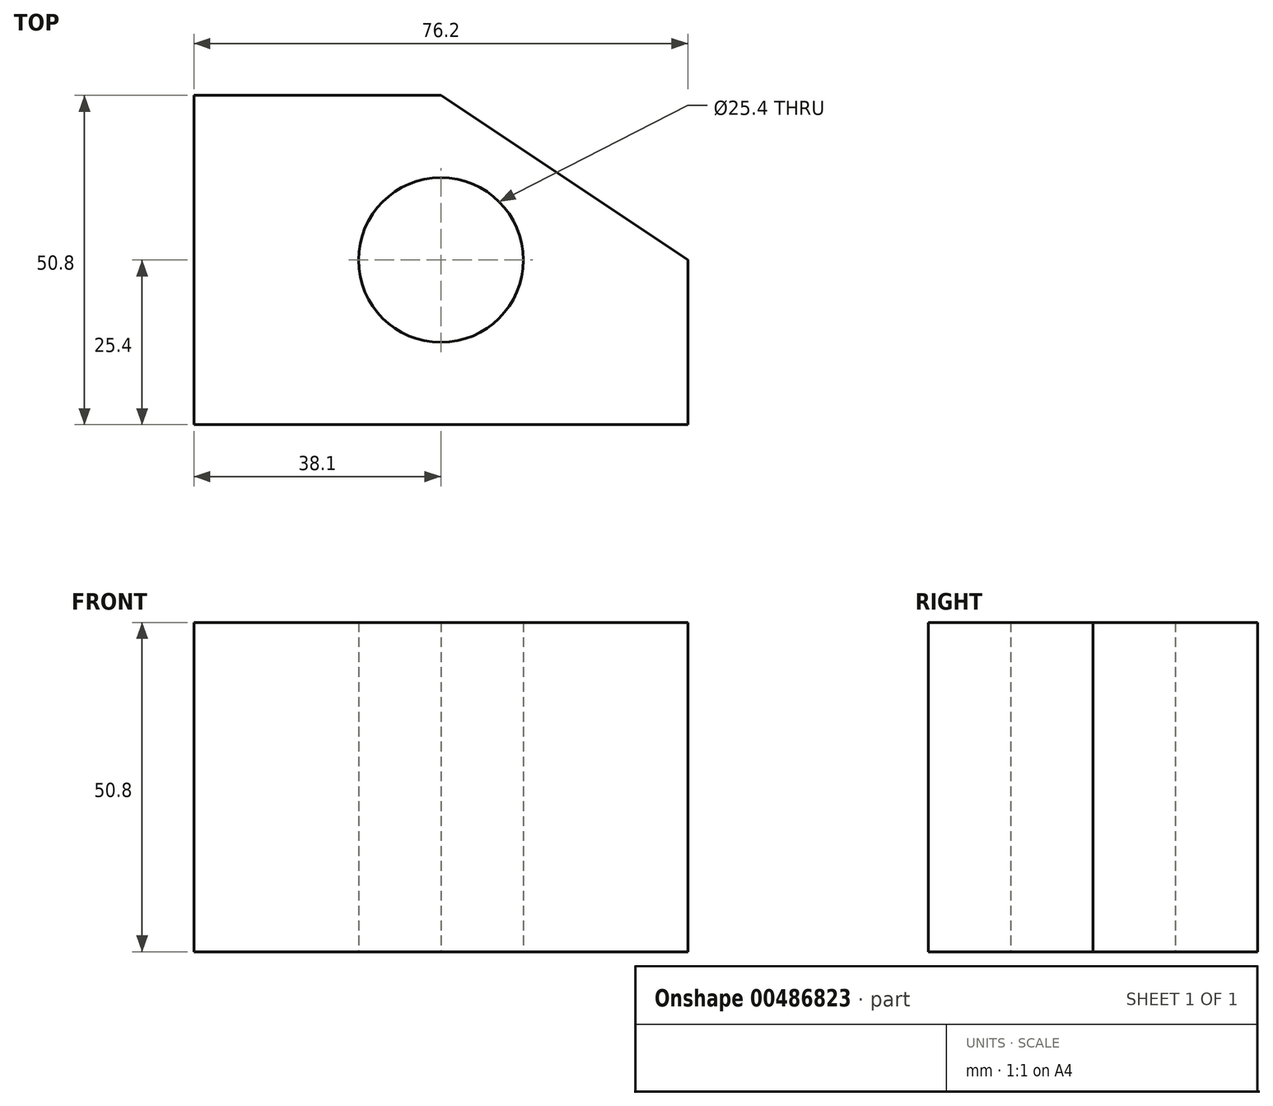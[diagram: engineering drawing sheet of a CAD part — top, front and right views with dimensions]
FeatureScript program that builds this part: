
annotation { "Feature Type Name" : "Feature", "Feature Type Description" : "" }
export const myFeature = defineFeature(function(context is Context, id is Id, definition is map)
    precondition{}
    {
        {
            var Q0;
            Q0=qCreatedBy(makeId("Top.planeOp"),FACE);
            var sketch = newSketch(context, id + "F0", { "sketchPlane" : qUnion([Q0])});
            skLineSegment(sketch, "E0.bottom", {"start": v(0, 0) * mm, "end": v(76.2, 0) * mm});
            skLineSegment(sketch, "E0.left", {"start": v(0, 0) * mm, "end": v(0, 25.4) * mm});
            skLineSegment(sketch, "E0.right", {"start": v(76.2, 0) * mm, "end": v(76.2, 25.4) * mm});
            skLineSegment(sketch, "E1.top", {"start": v(0, 50.8) * mm, "end": v(38.1, 50.8) * mm});
            skLineSegment(sketch, "E1.left", {"start": v(0, 25.4) * mm, "end": v(0, 50.8) * mm});
            skLineSegment(sketch, "E2", {"start": v(38.1, 50.8) * mm, "end": v(76.2, 25.4) * mm});
            skCircle(sketch, "E3", {"center": v(38.1, 25.4) * mm, "radius": 12.7 * mm});
            skPoint(sketch, "E3.centerSnap0", {"position": v(38.1, 0) * mm});
            skSolve(sketch);
        }
        {
            var Q0;
            Q0=makeQuery(id+"F0.imprint","IMPRINT",FACE,{"disambiguationData":[TD([[makeQuery(id+"F0.imprint","IMPRINT",EDGE,{"derivedFrom":sQuery(id+"F0.wireOp",EDGE,"E0.bottom")}),1.0]])]});
            extrude(context, id + "F1", {"entities" : qUnion([Q0]), "depth" : 50.8 * mm});
        }
    });
